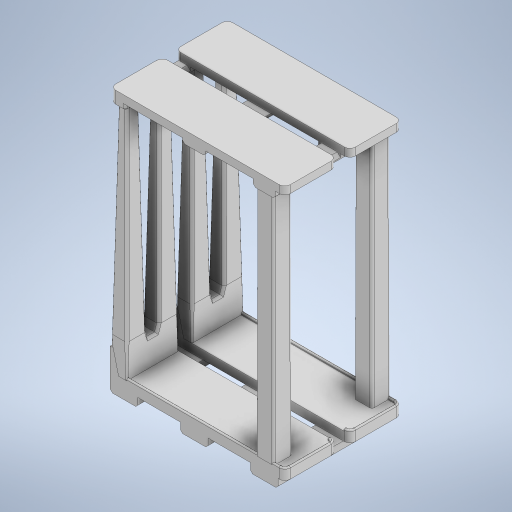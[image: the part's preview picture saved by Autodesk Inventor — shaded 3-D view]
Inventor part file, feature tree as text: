
AUTODESK INVENTOR PART (.ipt)
format: ipt  version: 2024.1 (Build 281209000, 209)  size: 1,486,848 bytes
history: native  units: mm
features: projected_geometry x43, extrude x23, sketch x23, chamfer x8, fillet x6, other x4, pattern_linear x1
ambient origin geometry x8: Origin, YZ Plane, XZ Plane, XY Plane, X Axis, Y Axis, Z Axis, Center Point
bodies: Body1 (feature_tree), Body2 (feature_tree), Body3 (feature_tree), Body4 (feature_tree)
feature tree (108):
  other  "span"
  extrude  "Extrusion1"  Depth=6.0mm
  extrude  "Extrusion2"  Depth=47.0mm
  sketch  "Sketch3"  dims[d4=158.0mm d5=8.0mm d6=0.0mm d7=152.0mm]
  sketch  "Sketch4"  dims[d8=25.0mm d9=25.0mm]
  extrude  "Extrusion4"  Depth=8.0mm TaperAngle=0.0deg
  fillet  "Fillet1"  Radius=152.0mm
  extrude  "Extrusion3"  Depth=25.0mm
  chamfer  "Chamfer1"  Distance=8.0mm
  fillet  "Fillet2"  Radius=15.0mm
  extrude  "Extrusion5"  Depth=17.0mm
  extrude  "Extrusion6"  Depth=220.0mm
  pattern_linear  "Rectangular Pattern1"  Count1=2 Spacing1=0.0mm
  fillet  "Fillet3"  Radius=2.5mm
  chamfer  "Chamfer2"  Distance=2.0mm Angle=45.0deg
  chamfer  "Chamfer3"  Distance=2.0mm Angle=45.0deg
  extrude  "Extrusion7"  Depth=2.5mm
  fillet  "Fillet4"  Radius=2.0mm
  extrude  "Extrusion9"  Depth=14.5mm
  extrude  "Extrusion10"  Depth=30.0mm TaperAngle=0.0deg
  sketch  "Sketch10"  dims[d21=14.0mm]
  extrude  "Extrusion11"  Depth=10.0mm TaperAngle=0.0deg
  extrude  "Extrusion12"  Depth=10.0mm TaperAngle=0.0deg
  extrude  "Extrusion13"  Depth=10.0mm TaperAngle=0.0deg
  extrude  "Extrusion14"  Depth=10.0mm TaperAngle=0.0deg
  extrude  "Extrusion15"  Depth=18.0mm
  extrude  "Extrusion16"  Depth=2.0mm
  extrude  "Extrusion17"  Depth=18.0mm
  chamfer  "Chamfer4"  Distance=18.0mm
  extrude  "Extrusion18"  Depth=18.0mm
  extrude  "Extrusion19"  Depth=10.0mm
  extrude  "Extrusion20"  Depth=6.0mm
  extrude  "Extrusion21"  Depth=2.0mm
  fillet  "Fillet5"  Radius=2.0mm
  fillet  "Fillet6"  Radius=2.0mm
  extrude  "Extrusion22"  Depth=2.0mm
  extrude  "Extrusion23"  TaperAngle=0.0deg  [1 undecoded]
  chamfer  "Chamfer5"  Distance=2.0mm Angle=45.0deg
  chamfer  "Chamfer6"  Distance=0.6mm
  chamfer  "Chamfer7"  Distance=0.6mm
  extrude  "Extrusion24"  Depth=10.0mm TaperAngle=0.0deg
  chamfer  "Chamfer8"  Distance=0.6mm
  sketch  "Sketch1"  dims[d0=6.0mm d1=6.0mm]
  sketch  "Sketch2"  dims[d2=47.0mm d3=47.0mm]
  projected_geometry  "Projected Loop1"
  other  "leggie-boys"
  sketch  "Sketch5"  dims[d10=25.0mm]
  projected_geometry  "Projected Loop2"
  projected_geometry  "Projected Loop3"
  sketch  "Sketch6"  dims[d11=38.5mm]
  projected_geometry  "Projected Loop4"
  sketch  "Sketch7"  dims[d12=38.5mm d13=8.0mm d14=0.0mm d15=15.0mm]
  projected_geometry  "Projected Loop5"
  projected_geometry  "Projected Loop6"
  sketch  "Sketch8"  dims[d16=17.0mm d17=17.0mm]
  projected_geometry  "Projected Loop7"
  projected_geometry  "Projected Loop8"
  sketch  "Sketch9"  dims[d18=17.0mm d19=220.0mm d20=-0.017453mm]
  projected_geometry  "Projected Loop9"
  other  "back-leggies"
  projected_geometry  "Projected Loop10"
  projected_geometry  "Projected Loop11"
  sketch  "Sketch11"  dims[d22=14.0mm]
  projected_geometry  "Projected Loop12"
  projected_geometry  "Projected Loop13"
  sketch  "Sketch12"  dims[d23=10.0mm]
  projected_geometry  "Projected Loop14"
  projected_geometry  "Projected Loop15"
  projected_geometry  "Projected Loop16"
  projected_geometry  "Projected Loop17"
  projected_geometry  "Projected Loop18"
  projected_geometry  "Projected Loop19"
  projected_geometry  "Projected Loop20"
  sketch  "Sketch13"  dims[d24=15.0mm d25=-0.349066mm]
  projected_geometry  "Projected Loop21"
  projected_geometry  "Projected Loop22"
  sketch  "Sketch14"  dims[d26=4.0mm]
  projected_geometry  "Projected Loop23"
  projected_geometry  "Projected Loop24"
  projected_geometry  "Projected Loop25"
  projected_geometry  "Projected Loop26"
  sketch  "Sketch15"  dims[d27=4.0mm]
  sketch  "Sketch16"  dims[d28=2.0mm]
  sketch  "Sketch17"  dims[d29=2.0mm d30=2.0mm d31=45.0deg]
  projected_geometry  "Projected Loop27"
  projected_geometry  "Projected Loop28"
  sketch  "Sketch18"  dims[d32=2.0mm d33=20.0mm d34=0.0mm d35=2.5mm d36=0.0mm]
  projected_geometry  "Projected Loop29"
  projected_geometry  "Projected Loop30"
  projected_geometry  "Projected Loop31"
  projected_geometry  "Projected Loop32"
  sketch  "Sketch19"  dims[d37=20.0mm d39=59.0mm d40=20.0mm d42=44.5mm]
  sketch  "Sketch20"  dims[d43=5.0mm d44=2.0mm d45=2.0mm d46=45.0deg d47=2.0mm d48=2.0mm d49=45.0deg]
  other  "hattie-boy"
  sketch  "Sketch22"  dims[d50=2.5mm d51=2.5mm d52=2.0mm d53=0.0mm]
  projected_geometry  "Projected Loop34"
  projected_geometry  "Projected Loop35"
  projected_geometry  "Projected Loop36"
  projected_geometry  "Projected Loop37"
  projected_geometry  "Projected Loop38"
  projected_geometry  "Projected Loop39"
  projected_geometry  "Projected Loop40"
  projected_geometry  "Projected Loop41"
  sketch  "Sketch23"  dims[d54=1.2mm d57=14.5mm d58=-0.349066mm]
  projected_geometry  "Projected Loop42"
  projected_geometry  "Projected Loop43"
  sketch  "Sketch25"  dims[d59=14.5mm d60=-0.349066mm d61=30.0mm d62=0.0mm d63=10.0mm d64=0.0mm d65=10.0mm d66=0.0mm d67=10.0mm d68=0.0mm d69=10.0mm d70=0.0mm d71=18.0mm d72=15.0mm d73=18.0mm d74=18.0mm d75=18.0mm d76=10.0mm d77=-0.174533mm d78=6.0mm d79=2.0mm d80=2.0mm d83=2.0mm d84=2.0mm d85=0.0mm d86=0.0mm d87=2.0mm d88=2.0mm d89=45.0deg d90=0.6mm d91=0.6mm d92=10.0mm d93=0.0mm d94=0.6mm d95=10.0mm d96=0.0mm d97=3.0mm d98=0.0mm d99=3.0mm d100=0.0mm d101=1.0mm d102=5.0mm d103=4.0mm d104=0.0mm d105=2.5mm d106=2.5mm d107=2.5mm d108=4.0mm d109=0.0mm d110=3.0mm d111=2.0mm d112=45.0deg d113=3.0mm d114=2.0mm d115=45.0deg d116=2.0mm d117=2.0mm d118=45.0deg d121=4.0mm d122=0.0mm d123=2.0mm d124=2.0mm d125=45.0deg]
  projected_geometry  "Projected Loop46"
note: 1 required parameter value undecoded (feature->parameter linkage not recoverable at this tier; creation-order binding heuristic only, values carry confidence <= 0.55)
